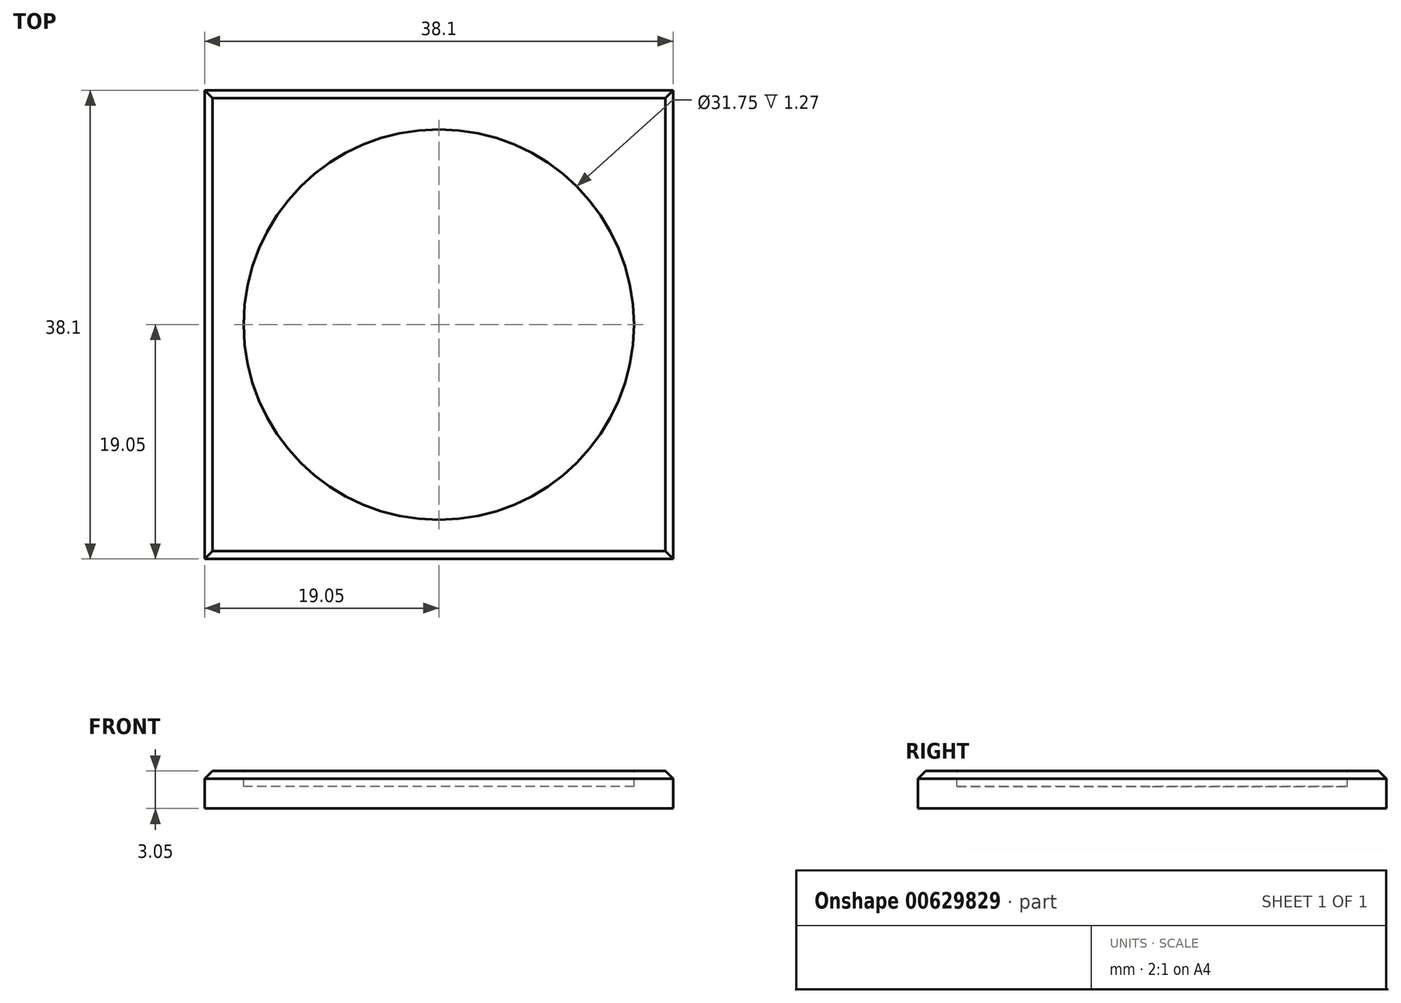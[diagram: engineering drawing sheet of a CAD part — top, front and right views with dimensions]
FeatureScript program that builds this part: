
annotation { "Feature Type Name" : "Feature", "Feature Type Description" : "" }
export const myFeature = defineFeature(function(context is Context, id is Id, definition is map)
    precondition{}
    {
        {
            var Q0;
            Q0=qCreatedBy(makeId("Top.planeOp"),FACE);
            var sketch = newSketch(context, id + "F0", { "sketchPlane" : qUnion([Q0])});
            skLineSegment(sketch, "E0.bottom", {"start": v(19.05, -19.05) * mm, "end": v(-19.05, -19.05) * mm});
            skLineSegment(sketch, "E0.top", {"start": v(19.05, 19.05) * mm, "end": v(-19.05, 19.05) * mm});
            skLineSegment(sketch, "E0.left", {"start": v(19.05, -19.05) * mm, "end": v(19.05, 19.05) * mm});
            skLineSegment(sketch, "E0.right", {"start": v(-19.05, -19.05) * mm, "end": v(-19.05, 19.05) * mm});
            skPoint(sketch, "E0.middle", {"position": v(0, 0) * mm});
            skSolve(sketch);
        }
        {
            var Q0;
            Q0=makeQuery(id+"F0.imprint","IMPRINT",FACE,{"disambiguationData":[TD([[makeQuery(id+"F0.imprint","IMPRINT",EDGE,{"derivedFrom":sQuery(id+"F0.wireOp",EDGE,"E0.bottom")}),-1.0]])]});
            extrude(context, id + "F1", {"entities" : qUnion([Q0]), "depth" : 3.05 * mm, "offsetDistance" : 25.4 * mm});
        }
        {
            var Q0;
            Q0=makeQuery(id+"F1.opExtrude","CAP_FACE",FACE,{"disambiguationData":[OSD([sQuery(id+"F0.wireOp",EDGE,"E0.bottom"),sQuery(id+"F0.wireOp",EDGE,"E0.top"),sQuery(id+"F0.wireOp",EDGE,"E0.left"),sQuery(id+"F0.wireOp",EDGE,"E0.right")])],"isStart":false});
            var sketch = newSketch(context, id + "F2", { "sketchPlane" : qUnion([Q0])});
            skCircle(sketch, "E1", {"center": v(0, 0) * mm, "radius": 15.88 * mm});
            skSolve(sketch);
        }
        {
            var Q0;
            Q0=makeQuery(id+"F2.imprint","IMPRINT",FACE,{"disambiguationData":[TD([[makeQuery(id+"F2.imprint","IMPRINT",EDGE,{"derivedFrom":sQuery(id+"F2.wireOp",EDGE,"E1")}),1.0]])]});
            extrude(context, id + "F3", {"entities" : qUnion([Q0]), "operationType" : NewBodyOperationType.REMOVE, "oppositeDirection" : true, "depth" : 1.27 * mm, "offsetDistance" : 25.4 * mm});
        }
        {
            var Q0;
            Q0=makeQuery(id+"F1.opExtrude","SWEPT_FACE",FACE,{"disambiguationData":[OSD([sQuery(id+"F0.wireOp",EDGE,"E0.bottom")])]});
            var sketch = newSketch(context, id + "F4", { "sketchPlane" : qUnion([Q0])});
            skLineSegment(sketch, "E2", {"start": v(-19.05, 3.05) * mm, "end": v(-19.05, 2.41) * mm});
            skLineSegment(sketch, "E3", {"start": v(-19.05, 2.41) * mm, "end": v(-18.42, 3.05) * mm});
            skLineSegment(sketch, "E4", {"start": v(-18.42, 3.05) * mm, "end": v(-19.05, 3.05) * mm});
            skLineSegment(sketch, "E5", {"start": v(19.05, 3.05) * mm, "end": v(18.41, 3.05) * mm});
            skLineSegment(sketch, "E6", {"start": v(18.41, 3.05) * mm, "end": v(19.05, 2.41) * mm});
            skLineSegment(sketch, "E7", {"start": v(19.05, 2.41) * mm, "end": v(19.05, 3.05) * mm});
            skSolve(sketch);
        }
        {
            var Q0;
            Q0=makeQuery(id+"F4.imprint","IMPRINT",FACE,{"disambiguationData":[TD([[makeQuery(id+"F4.imprint","IMPRINT",EDGE,{"derivedFrom":sQuery(id+"F4.wireOp",EDGE,"E2")}),1.0]])]});
            var Q1;
            Q1=makeQuery(id+"F4.imprint","IMPRINT",FACE,{"disambiguationData":[TD([[makeQuery(id+"F4.imprint","IMPRINT",EDGE,{"derivedFrom":sQuery(id+"F4.wireOp",EDGE,"E5")}),1.0]])]});
            var Q2;
            Q2=sQuery(id+"F4.wireOp",EDGE,"E4");
            var Q3;
            Q3=sQuery(id+"F4.wireOp",EDGE,"E2");
            var Q4;
            Q4=sQuery(id+"F4.wireOp",EDGE,"E3");
            var Q5;
            Q5=sQuery(id+"F4.wireOp",EDGE,"E6");
            var Q6;
            Q6=sQuery(id+"F4.wireOp",EDGE,"E7");
            var Q7;
            Q7=sQuery(id+"F4.wireOp",EDGE,"E5");
            extrude(context, id + "F5", {"entities" : qUnion([Q0, Q1]), "operationType" : NewBodyOperationType.REMOVE, "surfaceEntities" : qUnion([Q2, Q3, Q4, Q5, Q6, Q7]), "endBound" : BoundingType.THROUGH_ALL, "oppositeDirection" : true, "depth" : 25.4 * mm, "offsetDistance" : 25.4 * mm});
        }
        {
            var Q0;
            Q0=makeQuery(id+"F1.opExtrude","SWEPT_FACE",FACE,{"disambiguationData":[OSD([sQuery(id+"F0.wireOp",EDGE,"E0.right")])]});
            var sketch = newSketch(context, id + "F6", { "sketchPlane" : qUnion([Q0])});
            skLineSegment(sketch, "E8", {"start": v(-19.05, 3.05) * mm, "end": v(-19.05, 2.41) * mm});
            skLineSegment(sketch, "E9", {"start": v(-19.05, 2.41) * mm, "end": v(-18.41, 3.05) * mm});
            skLineSegment(sketch, "E10", {"start": v(-18.41, 3.05) * mm, "end": v(-19.05, 3.05) * mm});
            skLineSegment(sketch, "E11", {"start": v(19.05, 3.05) * mm, "end": v(18.42, 3.05) * mm});
            skLineSegment(sketch, "E12", {"start": v(18.42, 3.05) * mm, "end": v(19.05, 2.41) * mm});
            skLineSegment(sketch, "E13", {"start": v(19.05, 2.41) * mm, "end": v(19.05, 3.05) * mm});
            skSolve(sketch);
        }
        {
            var Q0;
            Q0=makeQuery(id+"F6.imprint","IMPRINT",FACE,{"disambiguationData":[TD([[makeQuery(id+"F6.imprint","IMPRINT",EDGE,{"derivedFrom":sQuery(id+"F6.wireOp",EDGE,"E8")}),1.0]])]});
            var Q1;
            Q1=makeQuery(id+"F6.imprint","IMPRINT",FACE,{"disambiguationData":[TD([[makeQuery(id+"F6.imprint","IMPRINT",EDGE,{"derivedFrom":sQuery(id+"F6.wireOp",EDGE,"E11")}),1.0]])]});
            extrude(context, id + "F7", {"entities" : qUnion([Q0, Q1]), "operationType" : NewBodyOperationType.REMOVE, "endBound" : BoundingType.THROUGH_ALL, "oppositeDirection" : true, "depth" : 25.4 * mm, "offsetDistance" : 25.4 * mm});
        }
    });
